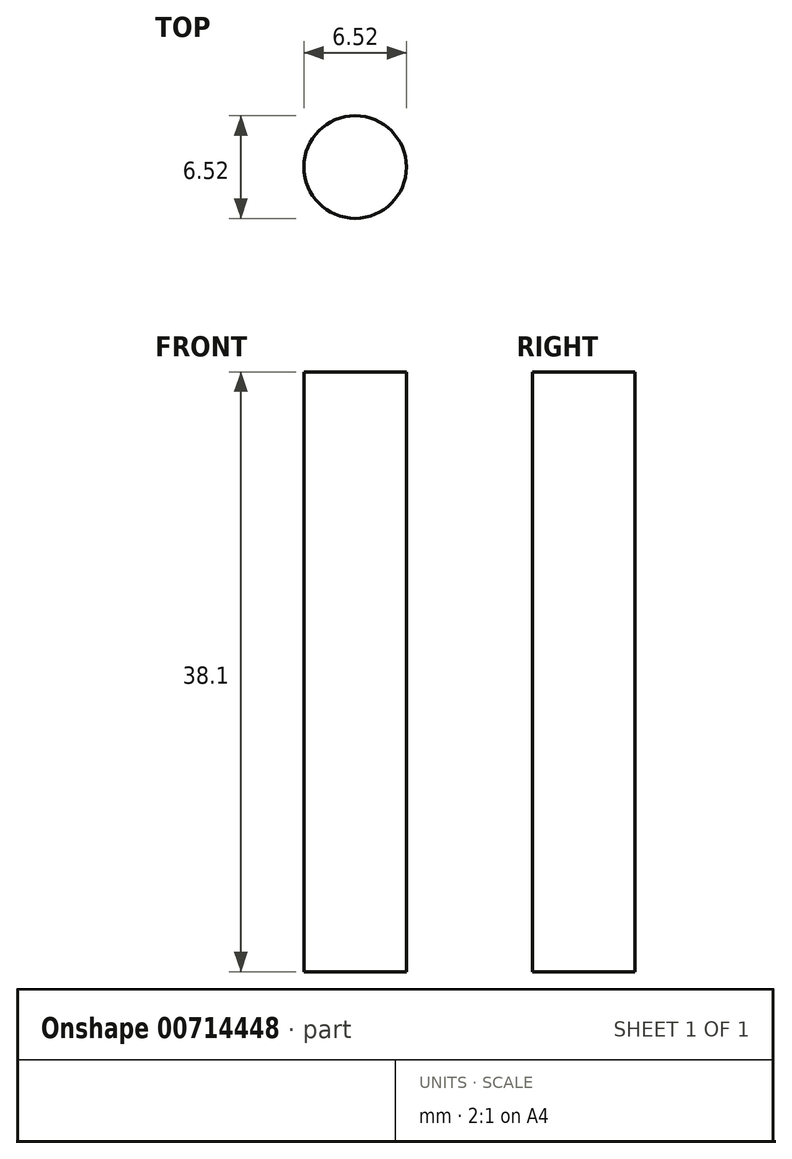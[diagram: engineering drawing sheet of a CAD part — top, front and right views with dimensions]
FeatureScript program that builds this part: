
annotation { "Feature Type Name" : "Feature", "Feature Type Description" : "" }
export const myFeature = defineFeature(function(context is Context, id is Id, definition is map)
    precondition{}
    {
        {
            var Q0;
            Q0=qCreatedBy(makeId("Top.planeOp"),FACE);
            var sketch = newSketch(context, id + "F0", { "sketchPlane" : qUnion([Q0])});
            skCircle(sketch, "E0", {"center": v(0, 0) * mm, "radius": 3.26 * mm});
            skSolve(sketch);
        }
        {
            var Q0;
            Q0=makeQuery(id+"F0.imprint","IMPRINT",FACE,{"disambiguationData":[TD([[makeQuery(id+"F0.imprint","IMPRINT",EDGE,{"derivedFrom":sQuery(id+"F0.wireOp",EDGE,"E0")}),1.0]])]});
            extrude(context, id + "F1", {"entities" : qUnion([Q0]), "depth" : 38.1 * mm});
        }
    });
